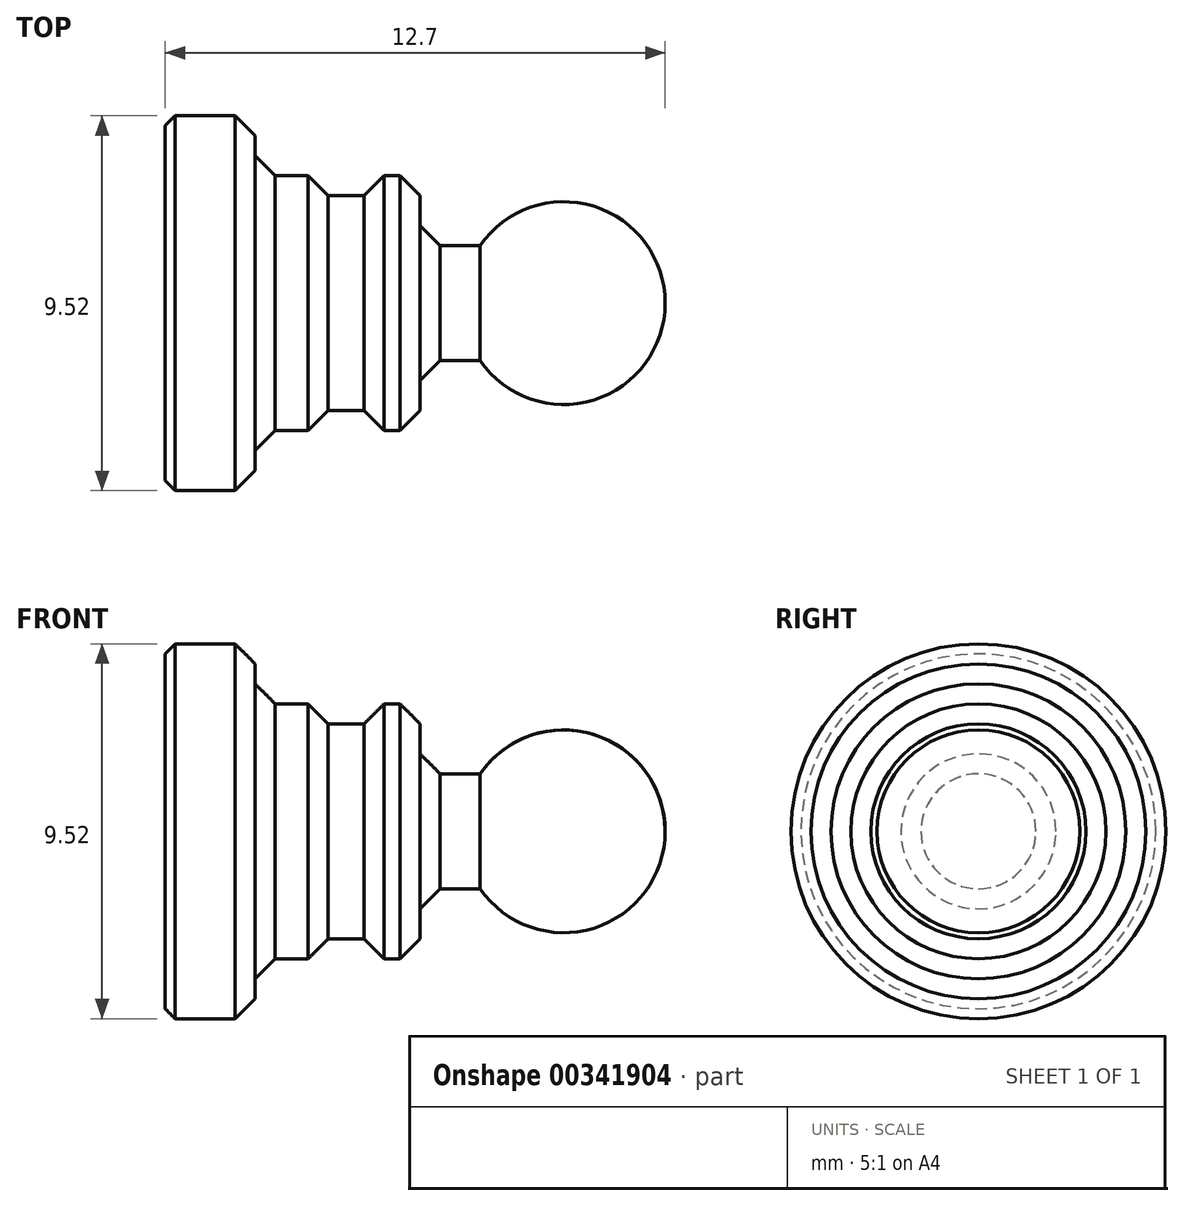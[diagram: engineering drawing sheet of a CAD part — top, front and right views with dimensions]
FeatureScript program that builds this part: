
annotation { "Feature Type Name" : "Feature", "Feature Type Description" : "" }
export const myFeature = defineFeature(function(context is Context, id is Id, definition is map)
    precondition{}
    {
        {
            var Q0;
            Q0=qCreatedBy(makeId("Front.planeOp"),FACE);
            var sketch = newSketch(context, id + "F0", { "sketchPlane" : qUnion([Q0])});
            skLineSegment(sketch, "E0", {"start": v(0, 0) * mm, "end": v(-12.7, 0) * mm});
            skLineSegment(sketch, "E1", {"start": v(-12.7, 0) * mm, "end": v(-12.7, 4.76) * mm});
            skLineSegment(sketch, "E2", {"start": v(-12.7, 4.76) * mm, "end": v(-10.41, 4.76) * mm});
            skLineSegment(sketch, "E3", {"start": v(-10.41, 4.76) * mm, "end": v(-10.41, 3.24) * mm});
            skLineSegment(sketch, "E4", {"start": v(-10.41, 3.24) * mm, "end": v(-8.56, 3.24) * mm});
            skLineSegment(sketch, "E5", {"start": v(-6.22, 3.24) * mm, "end": v(-6.22, 1.46) * mm});
            skLineSegment(sketch, "E6", {"start": v(-6.22, 1.46) * mm, "end": v(-4.7, 1.46) * mm});
            skArc(sketch, "E7", {"start": v(0, 0) * mm, "mid": v(-1.81, 2.46) * mm, "end": v(-4.7, 1.46) * mm});
            skLineSegment(sketch, "E8", {"start": v(-7.65, 3.24) * mm, "end": v(-7.65, 2.73) * mm});
            skLineSegment(sketch, "E9", {"start": v(-7.65, 2.73) * mm, "end": v(-8.56, 2.73) * mm});
            skLineSegment(sketch, "E10", {"start": v(-8.56, 2.73) * mm, "end": v(-8.56, 3.24) * mm});
            skLineSegment(sketch, "E11.trimOffspring", {"start": v(-7.65, 3.24) * mm, "end": v(-6.22, 3.24) * mm});
            skSolve(sketch);
        }
        {
            var Q0;
            Q0=makeQuery(id+"F0.imprint","IMPRINT",FACE,{"disambiguationData":[TD([[makeQuery(id+"F0.imprint","IMPRINT",EDGE,{"derivedFrom":sQuery(id+"F0.wireOp",EDGE,"E0")}),-1.0]])]});
            var Q1;
            Q1=sQuery(id+"F0.wireOp",EDGE,"E0");
            revolve(context, id + "F1", {"entities" : qUnion([Q0]), "axis" : qUnion([Q1]), "revolveType" : RevolveType.FULL});
        }
        {
            var Q0;
            Q0=makeQuery(id+"F1.opRevolve","SWEPT_EDGE",EDGE,{"disambiguationData":[OSD([sQuery(id+"F0.wireOp",EDGE,"E4"),sQuery(id+"F0.wireOp",EDGE,"E5")])]});
            var Q1;
            Q1=makeQuery(id+"F1.opRevolve","SWEPT_EDGE",EDGE,{"disambiguationData":[OSD([sQuery(id+"F0.wireOp",EDGE,"E2"),sQuery(id+"F0.wireOp",EDGE,"E3")])]});
            var Q2;
            Q2=makeQuery(id+"F1.opRevolve","SWEPT_EDGE",EDGE,{"disambiguationData":[OSD([sQuery(id+"F0.wireOp",EDGE,"E8"),sQuery(id+"F0.wireOp",EDGE,"E11.trimOffspring")])]});
            chamfer(context, id + "F2", {"entities" : qUnion([Q0, Q1, Q2]), "width" : 0.5 * mm, "tangentPropagation" : true});
        }
        {
            var Q0;
            Q0=makeQuery(id+"F1.opRevolve","SWEPT_EDGE",EDGE,{"disambiguationData":[OSD([sQuery(id+"F0.wireOp",EDGE,"E1"),sQuery(id+"F0.wireOp",EDGE,"E2")])]});
            chamfer(context, id + "F3", {"entities" : qUnion([Q0]), "width" : 0.25 * mm, "tangentPropagation" : true});
        }
    });
